# Revit family: Lighting Fixture Generic Model
name_source: partatom
category: Lighting Fixtures
units: mm (PartAtom-declared; Revit-internal decimal feet)

## family parameters
Always vertical = Yes
Cut with Voids When Loaded = No
Light Source = Yes
Maintain Annotation Orientation = No
OmniClass Number = 23.80.70.00
OmniClass Title = Lighting
Part Type = Normal
Room Calculation Point = No
Round Connector Dimension = Use Diameter
Shared = No
Work Plane-Based = No

## types (27) — shared parameters
CRI = 80
Color Filter = 16777215
Default Elevation = 8' - 0"
Dimming Lamp Color Temperature Shift = <None>
IP Rating = 65
Input Voltage = 120V-347V
Lamp = LED
Load Classification = Lighting
Manufacturer = Above All Lighting
Power Factor = 0.9
Tilt Angle = 90.00°
URL = https://www.abovealllighting.com
Upper Width = 0' - 1 15/16"

## per-type parameters (varying)
| type | Height | Length | Lower Width | Luminous Surface | Model | Photometric Web File | Wattage Comments |
| DSWP_9''_40SP_25W_3000K_T2 | 0' - 6 11/16" | 0' - 8 5/16" | 0' - 5 7/16" | 0' - 7 29/32" | DSWP-40SP-SW8-SD-BK | G3 cutt off Wall pack 25W 3000K T2_IESNA2002.IES | 25W |
| DSWP_9''_40SP_25W_3000K_T3 | 0' - 6 11/16" | 0' - 8 5/16" | 0' - 5 7/16" | 0' - 7 29/32" | DSWP-40SP-SW8-SD-BK | G3 cutt off Wall pack 25W 3000K T3_IESNA2002.IES | 25W |
| DSWP_9''_40SP_25W_3000K_T4 | 0' - 6 11/16" | 0' - 8 5/16" | 0' - 5 7/16" | 0' - 7 29/32" | DSWP-40SP-SW8-SD-BK | G3 cutt off Wall pack 25W 3000K T4_IESNA2002.IES | 25W |
| DSWP_14''_60SP_40W_3000K_T2 | 0' - 8 1/4" | 1' - 1 11/32" | 0' - 5 7/8" | 1' - 1 3/32" | DSWP-60SP-SW8-SD-BK | G3 cutt off Wall pack 40W 3000K T2_IESNA2002.IES | 40W |
| DSWP_9''_40SP_30W_3000K_T2 | 0' - 6 11/16" | 0' - 8 5/16" | 0' - 5 7/16" | 0' - 7 29/32" | DSWP-40SP-SW8-SD-BK | G3 cutt off Wall pack 30W 3000K T2_IESNA2002.IES | 30W |
| DSWP_9''_40SP_30W_3000K_T3 | 0' - 6 11/16" | 0' - 8 5/16" | 0' - 5 7/16" | 0' - 7 29/32" | DSWP-40SP-SW8-SD-BK | G3 cutt off Wall pack 30W 3000K T3_IESNA2002.IES | 30W |
| DSWP_9''_40SP_30W_3000K_T4 | 0' - 6 11/16" | 0' - 8 5/16" | 0' - 5 7/16" | 0' - 7 29/32" | DSWP-40SP-SW8-SD-BK | G3 cutt off Wall pack 30W 3000K T4_IESNA2002.IES | 30W |
| DSWP_9''_40SP_40W_3000K_T2 | 0' - 6 11/16" | 0' - 8 5/16" | 0' - 5 7/16" | 0' - 7 29/32" | DSWP-40SP-SW8-SD-BK | G3 cutt off Wall pack 40W 3000K T2_IESNA2002.IES | 40W |
| DSWP_9''_40SP_40W_3000K_T3 | 0' - 6 11/16" | 0' - 8 5/16" | 0' - 5 7/16" | 0' - 7 29/32" | DSWP-40SP-SW8-SD-BK | G3 cutt off Wall pack 40W 3000K T3_IESNA2002.IES | 40W |
| DSWP_9''_40SP_40W_3000K_T4 | 0' - 6 11/16" | 0' - 8 5/16" | 0' - 5 7/16" | 0' - 7 29/32" | DSWP-40SP-SW8-SD-BK | G3 cutt off Wall pack 40W 3000K T4_IESNA2002.IES | 40W |
| DSWP_14''_60SP_40W_3000K_T3 | 0' - 8 1/4" | 1' - 1 11/32" | 0' - 5 7/8" | 1' - 1 3/32" | DSWP-60SP-SW8-SD-BK | G3 cutt off Wall pack 40W 3000K T3_IESNA2002.IES | 40W |
| DSWP_14''_60SP_40W_3000K_T4 | 0' - 8 1/4" | 1' - 1 11/32" | 0' - 5 7/8" | 1' - 1 3/32" | DSWP-60SP-SW8-SD-BK | G3 cutt off Wall pack 40W 3000K T4_IESNA2002.IES | 40W |
| DSWP_14''_60SP_50W_3000K_T2 | 0' - 8 1/4" | 1' - 1 11/32" | 0' - 5 7/8" | 1' - 1 3/32" | DSWP-60SP-SW8-SD-BK | G3 cutt off Wall pack 50W 3000K T2_IESNA2002.IES | 50W |
| DSWP_14''_60SP_50W_3000K_T3 | 0' - 8 1/4" | 1' - 1 11/32" | 0' - 5 7/8" | 1' - 1 3/32" | DSWP-60SP-SW8-SD-BK | G3 cutt off Wall pack 50W 3000K T3_IESNA2002.IES | 50W |
| DSWP_14''_60SP_50W_3000K_T4 | 0' - 8 1/4" | 1' - 1 11/32" | 0' - 5 7/8" | 1' - 1 3/32" | DSWP-60SP-SW8-SD-BK | G3 cutt off Wall pack 50W 3000K T4_IESNA2002.IES | 50W |
| DSWP_14''_60SP_60W_3000K_T2 | 0' - 8 1/4" | 1' - 1 11/32" | 0' - 5 7/8" | 1' - 1 3/32" | DSWP-60SP-SW8-SD-BK | G3 cutt off Wall pack 60W 3000K T2_IESNA2002.IES | 60W |
| DSWP_14''_60SP_60W_3000K_T3 | 0' - 8 1/4" | 1' - 1 11/32" | 0' - 5 7/8" | 1' - 1 3/32" | DSWP-60SP-SW8-SD-BK | G3 cutt off Wall pack 60W 3000K T3_IESNA2002.IES | 60W |
| DSWP_14''_60SP_60W_3000K_T4 | 0' - 8 1/4" | 1' - 1 11/32" | 0' - 5 7/8" | 1' - 1 3/32" | DSWP-60SP-SW8-SD-BK | G3 cutt off Wall pack 60W 3000K T4_IESNA2002.IES | 60W |
| DSWP_14''_100SP_60W_3000K_T2 | 0' - 8 1/4" | 1' - 1 11/32" | 0' - 5 7/8" | 1' - 1 3/32" | DSWP-100SP-SW8-SD-BK | G3 cutt off Wall pack 60W 3000K T2_IESNA2002.IES | 60W |
| DSWP_14''_100SP_60W_3000K_T3 | 0' - 8 1/4" | 1' - 1 11/32" | 0' - 5 7/8" | 1' - 1 3/32" | DSWP-100SP-SW8-SD-BK | G3 cutt off Wall pack 60W 3000K T3_IESNA2002.IES | 60W |
| DSWP_14''_100SP_60W_3000K_T4 | 0' - 8 1/4" | 1' - 1 11/32" | 0' - 5 7/8" | 1' - 1 3/32" | DSWP-100SP-SW8-SD-BK | G3 cutt off Wall pack 60W 3000K T4_IESNA2002.IES | 60W |
| DSWP_14''_100SP_80W_3000K_T2 | 0' - 8 1/4" | 1' - 1 11/32" | 0' - 5 7/8" | 1' - 1 3/32" | DSWP-100SP-SW8-SD-BK | G3 cutt off Wall pack 80W 3000K T2_IESNA2002.IES | 80W |
| DSWP_14''_100SP_80W_3000K_T3 | 0' - 8 1/4" | 1' - 1 11/32" | 0' - 5 7/8" | 1' - 1 3/32" | DSWP-100SP-SW8-SD-BK | G3 cutt off Wall pack 80W 3000K T3_IESNA2002.IES | 80W |
| DSWP_14''_100SP_80W_3000K_T4 | 0' - 8 1/4" | 1' - 1 11/32" | 0' - 5 7/8" | 1' - 1 3/32" | DSWP-100SP-SW8-SD-BK | G3 cutt off Wall pack 80W 3000K T4_IESNA2002.IES | 80W |
| DSWP_14''_100SP_100W_3000K_T2 | 0' - 8 1/4" | 1' - 1 11/32" | 0' - 5 7/8" | 1' - 1 3/32" | DSWP-100SP-SW8-SD-BK | G3 cutt off Wall pack 100W 3000K T2_IESNA2002.IES | 100W |
| DSWP_14''_100SP_100W_3000K_T3 | 0' - 8 1/4" | 1' - 1 11/32" | 0' - 5 7/8" | 1' - 1 3/32" | DSWP-100SP-SW8-SD-BK | G3 cutt off Wall pack 100W 3000K T3_IESNA2002.IES | 100W |
| DSWP_14''_100SP_100W_3000K_T4 | 0' - 8 1/4" | 1' - 1 11/32" | 0' - 5 7/8" | 1' - 1 3/32" | DSWP-100SP-SW8-SD-BK | G3 cutt off Wall pack 100W 3000K T4_IESNA2002.IES | 100W |

## geometry (parser evidence)
native form markers: Sweep x2
no freeform markers — native parametric forms only
